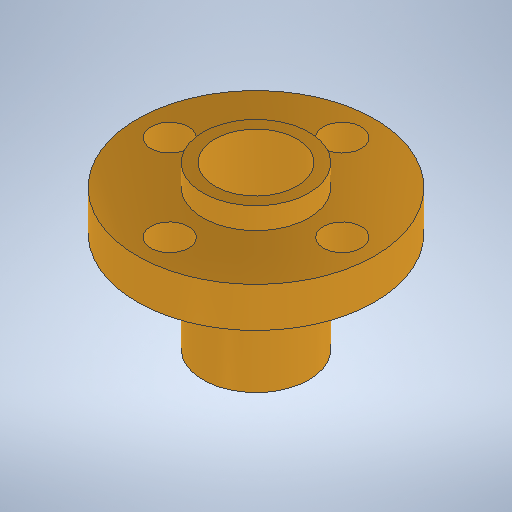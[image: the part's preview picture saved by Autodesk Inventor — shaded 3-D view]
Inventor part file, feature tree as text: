
AUTODESK INVENTOR PART (.ipt)
format: ipt  version: 2025.2 (Build 292293000, 293)  size: 281,600 bytes
history: native  units: mm
features: sketch x2, revolve x1, extrude x1, pattern_circular x1
ambient origin geometry x8: Origin, YZ Plane, XZ Plane, XY Plane, X Axis, Y Axis, Z Axis, Center Point
bodies: Solid1 (feature_tree)
feature tree (5):
  revolve  "Revolution1"  [1 undecoded]
  extrude  "Extrusion1"  Depth=11.0mm
  pattern_circular  "Circular Pattern1"  [2 undecoded]
  sketch  "Sketch1"  dims[d0=3.7mm d1=15.0mm]
  sketch  "Sketch2"  dims[d2=2.0mm d3=11.0mm d4=6.1mm d5=3.8mm d6=90.0deg d7=3.5mm d8=8.0mm d9=10.0mm d10=0.0mm d11=40.0mm d12=360.0deg]
note: 3 required parameter values undecoded (feature->parameter linkage not recoverable at this tier; creation-order binding heuristic only, values carry confidence <= 0.55)